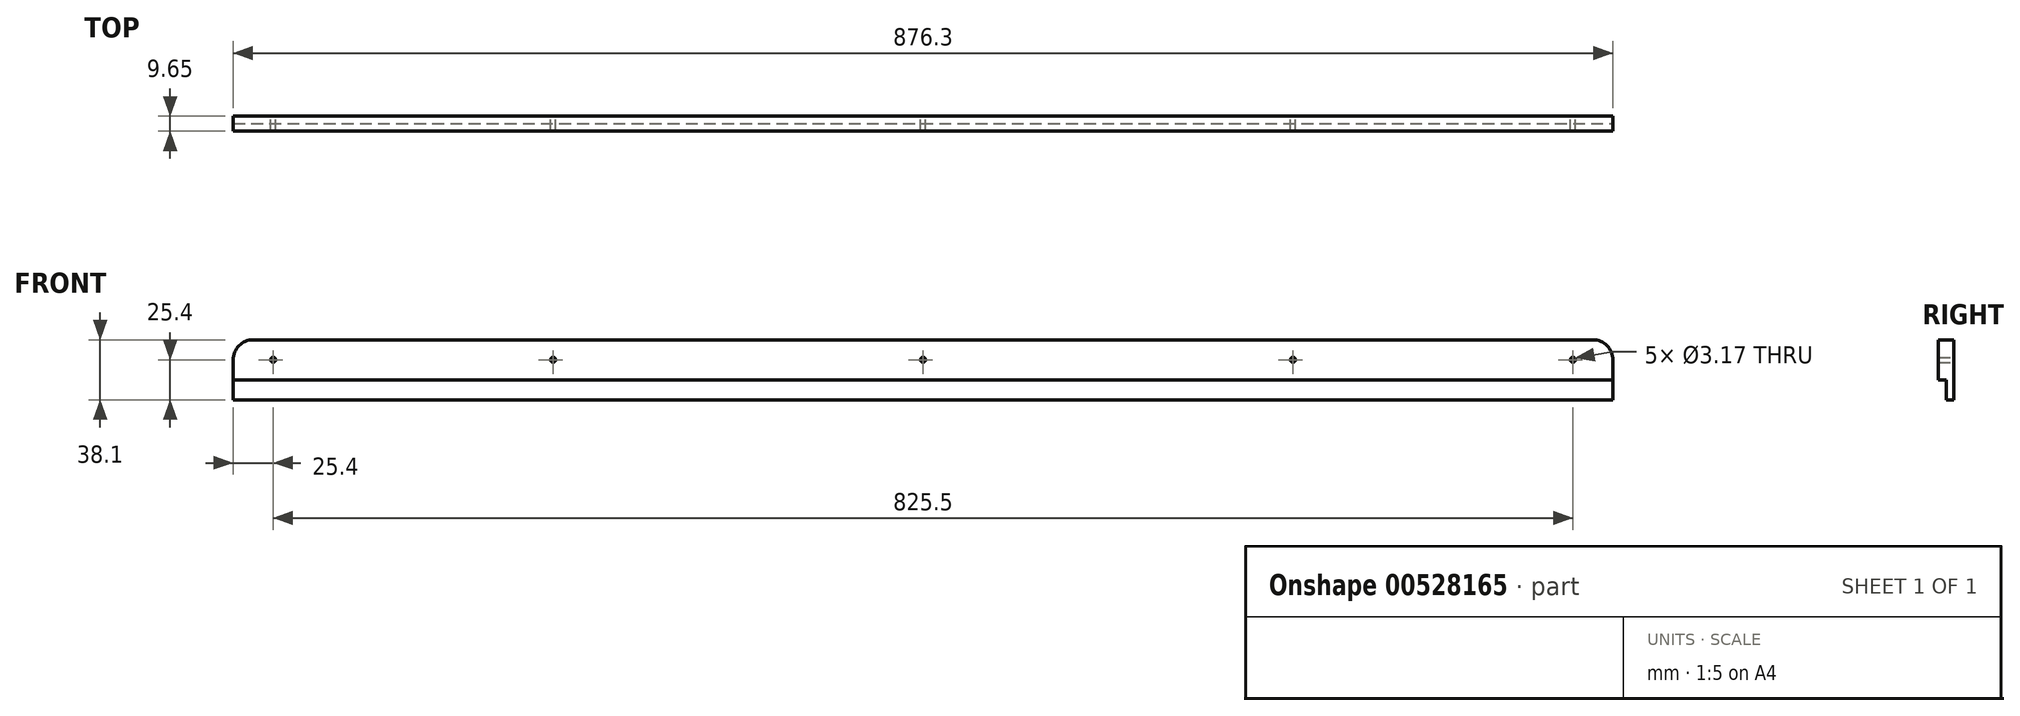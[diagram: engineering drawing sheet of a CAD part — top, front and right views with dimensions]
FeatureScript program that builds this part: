
annotation { "Feature Type Name" : "Feature", "Feature Type Description" : "" }
export const myFeature = defineFeature(function(context is Context, id is Id, definition is map)
    precondition{}
    {
        {
            var Q0;
            Q0=qCreatedBy(makeId("Front.planeOp"),FACE);
            var sketch = newSketch(context, id + "F0", { "sketchPlane" : qUnion([Q0])});
            skLineSegment(sketch, "E0.bottom", {"start": v(-438.15, -19.05) * mm, "end": v(438.15, -19.05) * mm});
            skLineSegment(sketch, "E0.top", {"start": v(-438.15, 19.05) * mm, "end": v(438.15, 19.05) * mm});
            skLineSegment(sketch, "E0.left", {"start": v(-438.15, -19.05) * mm, "end": v(-438.15, 19.05) * mm});
            skLineSegment(sketch, "E0.right", {"start": v(438.15, -19.05) * mm, "end": v(438.15, 19.05) * mm});
            skPoint(sketch, "E0.middle", {"position": v(0, 0) * mm});
            skSolve(sketch);
        }
        {
            var Q0;
            Q0=makeQuery(id+"F0.imprint","IMPRINT",FACE,{"disambiguationData":[TD([[makeQuery(id+"F0.imprint","IMPRINT",EDGE,{"derivedFrom":sQuery(id+"F0.wireOp",EDGE,"E0.bottom")}),1.0]])]});
            extrude(context, id + "F1", {"entities" : qUnion([Q0]), "depth" : 9.65 * mm, "offsetDistance" : 25.4 * mm});
        }
        {
            var Q0;
            Q0=makeQuery(id+"F1.opExtrude","CAP_FACE",FACE,{"disambiguationData":[OSD([sQuery(id+"F0.wireOp",EDGE,"E0.bottom"),sQuery(id+"F0.wireOp",EDGE,"E0.top"),sQuery(id+"F0.wireOp",EDGE,"E0.left"),sQuery(id+"F0.wireOp",EDGE,"E0.right")])],"isStart":true});
            var sketch = newSketch(context, id + "F2", { "sketchPlane" : qUnion([Q0])});
            skLineSegment(sketch, "E1", {"start": v(-438.15, 19.05) * mm, "end": v(-438.15, 6.35) * mm});
            skLineSegment(sketch, "E2", {"start": v(-438.15, 6.35) * mm, "end": v(438.15, 6.35) * mm});
            skLineSegment(sketch, "E3", {"start": v(438.15, 6.35) * mm, "end": v(412.75, 6.35) * mm});
            skLineSegment(sketch, "E4", {"start": v(412.75, 6.35) * mm, "end": v(0, 6.35) * mm});
            skLineSegment(sketch, "E5", {"start": v(-438.15, 6.35) * mm, "end": v(-412.75, 6.35) * mm});
            skLineSegment(sketch, "E6", {"start": v(-412.75, 6.35) * mm, "end": v(-234.95, 6.35) * mm});
            skLineSegment(sketch, "E7", {"start": v(412.75, 6.35) * mm, "end": v(234.95, 6.35) * mm});
            skPoint(sketch, "E8", {"position": v(-412.75, 6.35) * mm});
            skPoint(sketch, "E9", {"position": v(-234.95, 6.35) * mm});
            skPoint(sketch, "E10", {"position": v(0, 6.35) * mm});
            skPoint(sketch, "E11", {"position": v(234.95, 6.35) * mm});
            skPoint(sketch, "E12", {"position": v(412.75, 6.35) * mm});
            skSolve(sketch);
        }
        {
            var Q0;
            Q0=sQuery(id+"F2.wireOp",VERTEX,"E8");
            var Q1;
            Q1=sQuery(id+"F2.wireOp",VERTEX,"E9");
            var Q2;
            Q2=sQuery(id+"F2.wireOp",VERTEX,"E10");
            var Q3;
            Q3=sQuery(id+"F2.wireOp",VERTEX,"E11");
            var Q4;
            Q4=sQuery(id+"F2.wireOp",VERTEX,"E12");
            var Q5;
            Q5=makeQuery(id+"F1.opExtrude","SWEPT_BODY",BODY,{"disambiguationData":[OSD([sQuery(id+"F0.wireOp",EDGE,"E0.bottom"),sQuery(id+"F0.wireOp",EDGE,"E0.top"),sQuery(id+"F0.wireOp",EDGE,"E0.left"),sQuery(id+"F0.wireOp",EDGE,"E0.right")])]});
            hole(context, id + "F3", {"style" : HoleStyle.SIMPLE, "endStyle" : HoleEndStyle.BLIND, "holeDiameter" : 3.17 * mm, "holeDepth" : 9.65 * mm, "isTappedThrough" : true, "tappedDepth" : 12.7 * mm, "tapClearance" : 3, "startFromSketch" : true, "locations" : qUnion([Q0, Q1, Q2, Q3, Q4]), "scope" : qUnion([Q5])});
        }
        {
            var Q0;
            Q0=makeQuery(id+"F1.opExtrude","SWEPT_EDGE",EDGE,{"disambiguationData":[OSD([sQuery(id+"F0.wireOp",EDGE,"E0.top"),sQuery(id+"F0.wireOp",EDGE,"E0.right")])]});
            fillet(context, id + "F4", {"entities" : qUnion([Q0]), "radius" : 12.7 * mm, "tangentPropagation" : true, "allowEdgeOverflow" : false});
        }
        {
            var Q0;
            Q0=makeQuery(id+"F1.opExtrude","SWEPT_EDGE",EDGE,{"disambiguationData":[OSD([sQuery(id+"F0.wireOp",EDGE,"E0.top"),sQuery(id+"F0.wireOp",EDGE,"E0.left")])]});
            fillet(context, id + "F5", {"entities" : qUnion([Q0]), "radius" : 12.7 * mm, "tangentPropagation" : true, "allowEdgeOverflow" : false});
        }
        {
            var Q0;
            Q0=makeQuery(id+"F1.opExtrude","CAP_FACE",FACE,{"disambiguationData":[OSD([sQuery(id+"F0.wireOp",EDGE,"E0.bottom"),sQuery(id+"F0.wireOp",EDGE,"E0.top"),sQuery(id+"F0.wireOp",EDGE,"E0.left"),sQuery(id+"F0.wireOp",EDGE,"E0.right")])],"isStart":false});
            var sketch = newSketch(context, id + "F6", { "sketchPlane" : qUnion([Q0])});
            skLineSegment(sketch, "E13", {"start": v(-438.15, -19.05) * mm, "end": v(-438.15, -6.35) * mm});
            skLineSegment(sketch, "E14", {"start": v(-438.15, -6.35) * mm, "end": v(438.15, -6.35) * mm});
            skSolve(sketch);
        }
        {
            var Q0;
            Q0=makeQuery(id+"F6.imprint","IMPRINT",FACE,{"disambiguationData":[TD([[makeQuery(id+"F6.imprint","IMPRINT",EDGE,{"derivedFrom":sQuery(id+"F6.wireOp",EDGE,"E13")}),-1.0]])]});
            extrude(context, id + "F7", {"entities" : qUnion([Q0]), "operationType" : NewBodyOperationType.REMOVE, "oppositeDirection" : true, "depth" : 4.83 * mm, "offsetDistance" : 25.4 * mm});
        }
    });
